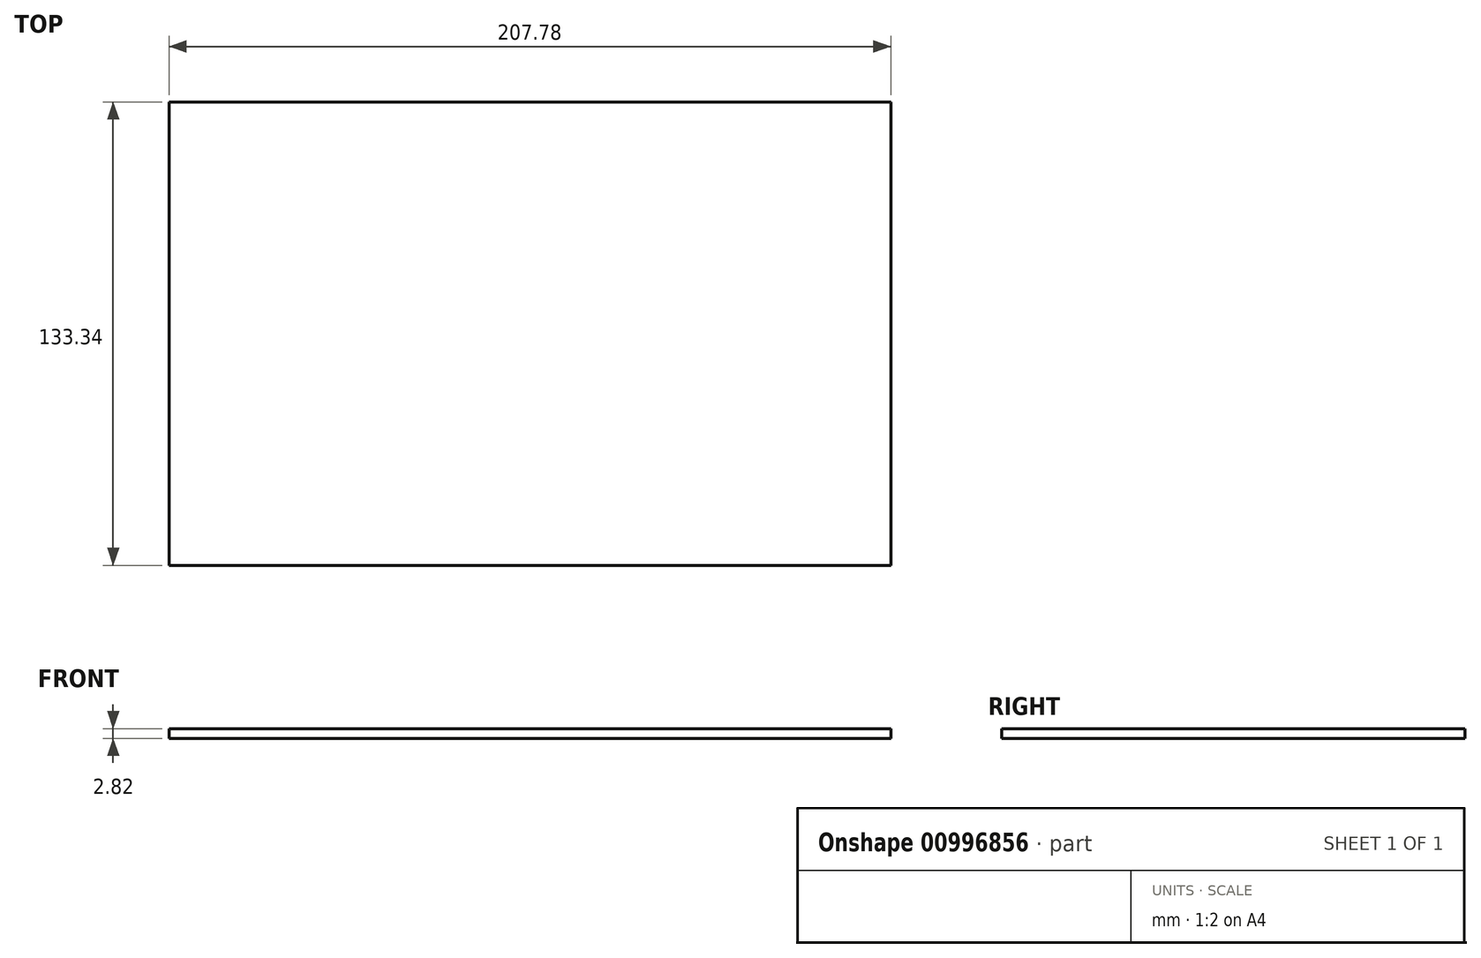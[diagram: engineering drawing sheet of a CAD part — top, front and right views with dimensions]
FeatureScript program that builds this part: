
annotation { "Feature Type Name" : "Feature", "Feature Type Description" : "" }
export const myFeature = defineFeature(function(context is Context, id is Id, definition is map)
    precondition{}
    {
        {
            var Q0;
            Q0=qCreatedBy(makeId("Top.planeOp"),FACE);
            var sketch = newSketch(context, id + "F0", { "sketchPlane" : qUnion([Q0])});
            skLineSegment(sketch, "E0.bottom", {"start": v(103.89, -66.67) * mm, "end": v(-103.89, -66.68) * mm});
            skLineSegment(sketch, "E0.top", {"start": v(103.89, 66.68) * mm, "end": v(-103.89, 66.67) * mm});
            skLineSegment(sketch, "E0.left", {"start": v(103.89, -66.67) * mm, "end": v(103.89, 66.68) * mm});
            skLineSegment(sketch, "E0.right", {"start": v(-103.89, -66.68) * mm, "end": v(-103.89, 66.68) * mm});
            skPoint(sketch, "E0.middle", {"position": v(0, 0) * mm});
            skSolve(sketch);
        }
        {
            var Q0;
            Q0=qSketchRegion(id+"F0",true);
            extrude(context, id + "F1", {"entities" : qUnion([Q0]), "depth" : 2.82 * mm, "offsetDistance" : 25.4 * mm});
        }
    });
